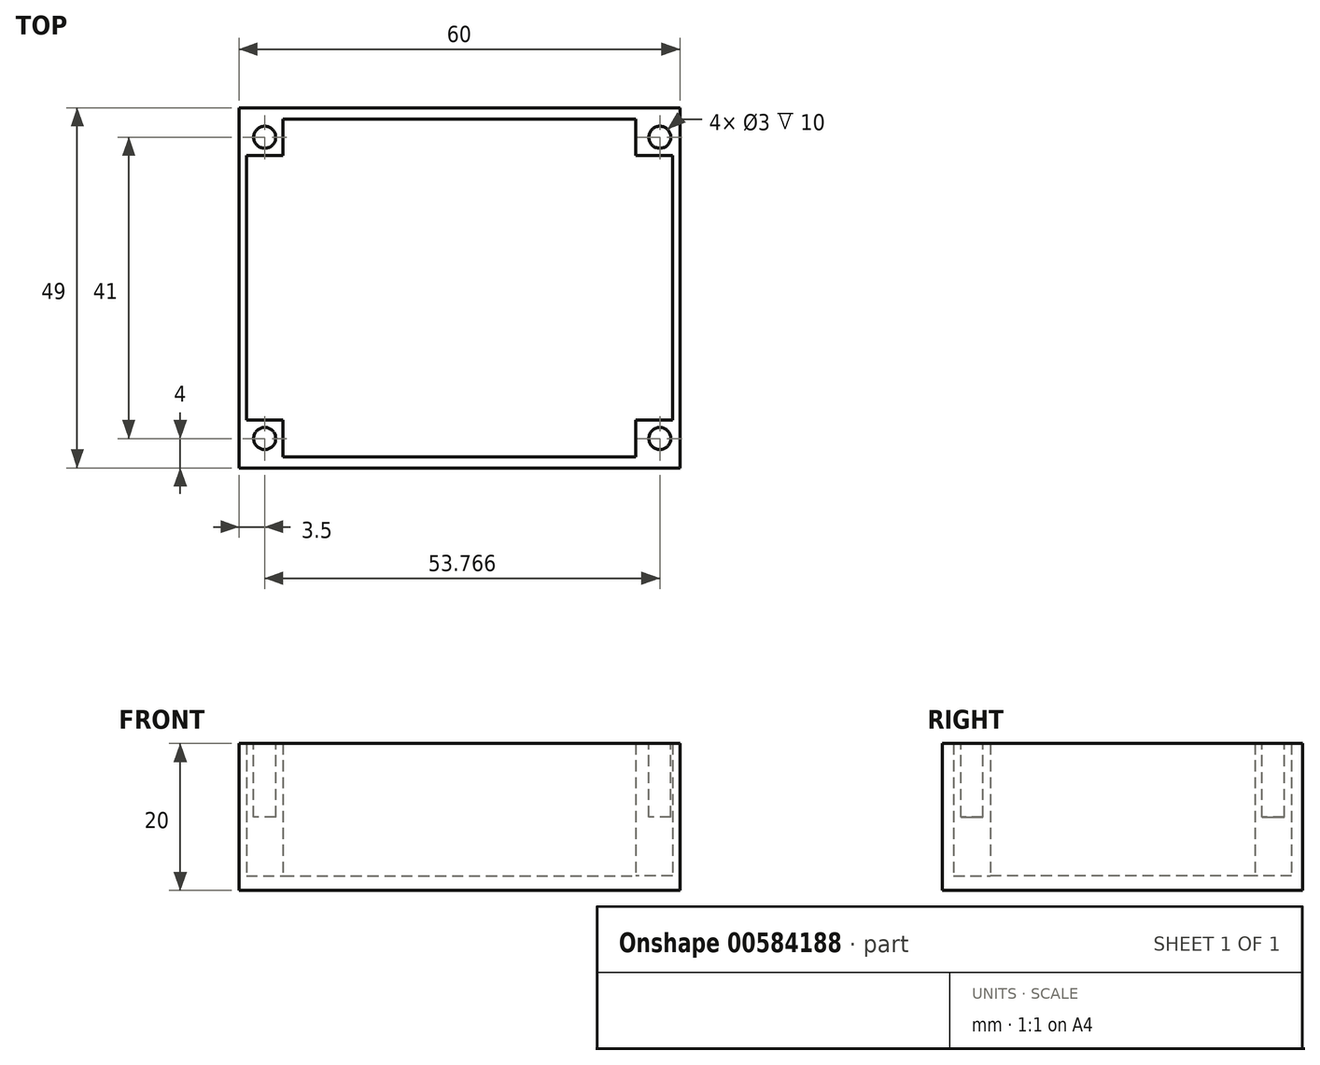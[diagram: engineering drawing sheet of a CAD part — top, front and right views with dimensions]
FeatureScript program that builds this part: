
annotation { "Feature Type Name" : "Feature", "Feature Type Description" : "" }
export const myFeature = defineFeature(function(context is Context, id is Id, definition is map)
    precondition{}
    {
        {
            var Q0;
            Q0=qCreatedBy(makeId("Top.planeOp"),FACE);
            var sketch = newSketch(context, id + "F0", { "sketchPlane" : qUnion([Q0])});
            skLineSegment(sketch, "E0.bottom", {"start": v(-30, 24.5) * mm, "end": v(30, 24.5) * mm});
            skLineSegment(sketch, "E0.top", {"start": v(-30, -24.5) * mm, "end": v(30, -24.5) * mm});
            skLineSegment(sketch, "E0.left", {"start": v(-30, 24.5) * mm, "end": v(-30, -24.5) * mm});
            skLineSegment(sketch, "E0.right", {"start": v(30, 24.5) * mm, "end": v(30, -24.5) * mm});
            skPoint(sketch, "E0.middle", {"position": v(0, 0) * mm});
            skSolve(sketch);
        }
        {
            var Q0;
            Q0=makeQuery(id+"F0.imprint","IMPRINT",FACE,{"disambiguationData":[TD([[makeQuery(id+"F0.imprint","IMPRINT",EDGE,{"derivedFrom":sQuery(id+"F0.wireOp",EDGE,"E0.bottom")}),-1.0]])]});
            extrude(context, id + "F1", {"entities" : qUnion([Q0]), "depth" : 20 * mm, "offsetDistance" : 25 * mm});
        }
        {
            var Q0;
            Q0=makeQuery(id+"F1.opExtrude","CAP_FACE",FACE,{"disambiguationData":[OSD([sQuery(id+"F0.wireOp",EDGE,"E0.bottom"),sQuery(id+"F0.wireOp",EDGE,"E0.top"),sQuery(id+"F0.wireOp",EDGE,"E0.left"),sQuery(id+"F0.wireOp",EDGE,"E0.right")])],"isStart":false});
            var sketch = newSketch(context, id + "F2", { "sketchPlane" : qUnion([Q0])});
            skLineSegment(sketch, "E1.bottom", {"start": v(-29, 23) * mm, "end": v(29, 23) * mm});
            skLineSegment(sketch, "E1.top", {"start": v(-29, -23) * mm, "end": v(29, -23) * mm});
            skLineSegment(sketch, "E1.left", {"start": v(-29, 23) * mm, "end": v(-29, -23) * mm});
            skLineSegment(sketch, "E1.right", {"start": v(29, 23) * mm, "end": v(29, -23) * mm});
            skPoint(sketch, "E1.middle", {"position": v(0, 0) * mm});
            skSolve(sketch);
        }
        {
            var Q0;
            Q0=makeQuery(id+"F2.imprint","IMPRINT",FACE,{"disambiguationData":[TD([[makeQuery(id+"F2.imprint","IMPRINT",EDGE,{"derivedFrom":sQuery(id+"F2.wireOp",EDGE,"E1.bottom")}),-1.0]])]});
            extrude(context, id + "F3", {"entities" : qUnion([Q0]), "operationType" : NewBodyOperationType.REMOVE, "oppositeDirection" : true, "depth" : 18 * mm, "offsetDistance" : 25 * mm});
        }
        {
            var Q0;
            Q0=makeQuery(id+"F3.boolean.opBoolean","COPY",FACE,{"derivedFrom":makeQuery(id+"F3.opExtrude","CAP_FACE",FACE,{"disambiguationData":[OSD([sQuery(id+"F2.wireOp",EDGE,"E1.bottom"),sQuery(id+"F2.wireOp",EDGE,"E1.top"),sQuery(id+"F2.wireOp",EDGE,"E1.left"),sQuery(id+"F2.wireOp",EDGE,"E1.right")])],"isStart":false})});
            var sketch = newSketch(context, id + "F4", { "sketchPlane" : qUnion([Q0])});
            skLineSegment(sketch, "E2.bottom", {"start": v(29, 23) * mm, "end": v(24, 23) * mm});
            skLineSegment(sketch, "E2.top", {"start": v(29, 18) * mm, "end": v(24, 18) * mm});
            skLineSegment(sketch, "E2.left", {"start": v(29, 23) * mm, "end": v(29, 18) * mm});
            skLineSegment(sketch, "E2.right", {"start": v(24, 23) * mm, "end": v(24, 18) * mm});
            skLineSegment(sketch, "E3.bottom", {"start": v(29, -23) * mm, "end": v(24, -23) * mm});
            skLineSegment(sketch, "E3.top", {"start": v(29, -18) * mm, "end": v(24, -18) * mm});
            skLineSegment(sketch, "E3.left", {"start": v(29, -23) * mm, "end": v(29, -18) * mm});
            skLineSegment(sketch, "E3.right", {"start": v(24, -23) * mm, "end": v(24, -18) * mm});
            skLineSegment(sketch, "E4.bottom", {"start": v(-29, -23) * mm, "end": v(-24, -23) * mm});
            skLineSegment(sketch, "E4.top", {"start": v(-29, -18) * mm, "end": v(-24, -18) * mm});
            skLineSegment(sketch, "E4.left", {"start": v(-29, -23) * mm, "end": v(-29, -18) * mm});
            skLineSegment(sketch, "E4.right", {"start": v(-24, -23) * mm, "end": v(-24, -18) * mm});
            skLineSegment(sketch, "E5.bottom", {"start": v(-29, 23) * mm, "end": v(-24, 23) * mm});
            skLineSegment(sketch, "E5.top", {"start": v(-29, 18) * mm, "end": v(-24, 18) * mm});
            skLineSegment(sketch, "E5.left", {"start": v(-29, 23) * mm, "end": v(-29, 18) * mm});
            skLineSegment(sketch, "E5.right", {"start": v(-24, 23) * mm, "end": v(-24, 18) * mm});
            skSolve(sketch);
        }
        {
            var Q0;
            Q0=makeQuery(id+"F4.imprint","IMPRINT",FACE,{"disambiguationData":[TD([[makeQuery(id+"F4.imprint","IMPRINT",EDGE,{"derivedFrom":sQuery(id+"F4.wireOp",EDGE,"E4.bottom")}),1.0]])]});
            var Q1;
            Q1=makeQuery(id+"F4.imprint","IMPRINT",FACE,{"disambiguationData":[TD([[makeQuery(id+"F4.imprint","IMPRINT",EDGE,{"derivedFrom":sQuery(id+"F4.wireOp",EDGE,"E3.bottom")}),1.0]])]});
            var Q2;
            Q2=makeQuery(id+"F4.imprint","IMPRINT",FACE,{"disambiguationData":[TD([[makeQuery(id+"F4.imprint","IMPRINT",EDGE,{"derivedFrom":sQuery(id+"F4.wireOp",EDGE,"E5.bottom")}),-1.0]])]});
            var Q3;
            Q3=makeQuery(id+"F4.imprint","IMPRINT",FACE,{"disambiguationData":[TD([[makeQuery(id+"F4.imprint","IMPRINT",EDGE,{"derivedFrom":sQuery(id+"F4.wireOp",EDGE,"E2.bottom")}),-1.0]])]});
            extrude(context, id + "F5", {"entities" : qUnion([Q0, Q1, Q2, Q3]), "operationType" : NewBodyOperationType.ADD, "depth" : 18 * mm, "offsetDistance" : 25 * mm});
        }
        {
            var Q0;
            Q0=makeQuery(id+"F5.boolean.opBoolean","MERGE",FACE,{"derivedFrom":[makeQuery(id+"F1.opExtrude","CAP_FACE",FACE,{"disambiguationData":[OSD([sQuery(id+"F0.wireOp",EDGE,"E0.bottom"),sQuery(id+"F0.wireOp",EDGE,"E0.top"),sQuery(id+"F0.wireOp",EDGE,"E0.left"),sQuery(id+"F0.wireOp",EDGE,"E0.right")])],"isStart":false}),makeQuery(id+"F5.opExtrude","CAP_FACE",FACE,{"disambiguationData":[OSD([sQuery(id+"F4.wireOp",EDGE,"E2.bottom"),sQuery(id+"F4.wireOp",EDGE,"E2.top"),sQuery(id+"F4.wireOp",EDGE,"E2.left"),sQuery(id+"F4.wireOp",EDGE,"E2.right")])],"isStart":false}),makeQuery(id+"F5.opExtrude","CAP_FACE",FACE,{"disambiguationData":[OSD([sQuery(id+"F4.wireOp",EDGE,"E3.bottom"),sQuery(id+"F4.wireOp",EDGE,"E3.top"),sQuery(id+"F4.wireOp",EDGE,"E3.left"),sQuery(id+"F4.wireOp",EDGE,"E3.right")])],"isStart":false}),makeQuery(id+"F5.opExtrude","CAP_FACE",FACE,{"disambiguationData":[OSD([sQuery(id+"F4.wireOp",EDGE,"E4.bottom"),sQuery(id+"F4.wireOp",EDGE,"E4.top"),sQuery(id+"F4.wireOp",EDGE,"E4.left"),sQuery(id+"F4.wireOp",EDGE,"E4.right")])],"isStart":false}),makeQuery(id+"F5.opExtrude","CAP_FACE",FACE,{"disambiguationData":[OSD([sQuery(id+"F4.wireOp",EDGE,"E5.bottom"),sQuery(id+"F4.wireOp",EDGE,"E5.top"),sQuery(id+"F4.wireOp",EDGE,"E5.left"),sQuery(id+"F4.wireOp",EDGE,"E5.right")])],"isStart":false})]});
            var sketch = newSketch(context, id + "F6", { "sketchPlane" : qUnion([Q0])});
            skCircle(sketch, "E6", {"center": v(-26.5, -20.5) * mm, "radius": 1.5 * mm});
            skPoint(sketch, "E6.centerSnap0", {"position": v(-24, -20.5) * mm});
            skPoint(sketch, "E6.centerSnap1", {"position": v(-26.5, -18) * mm});
            skCircle(sketch, "E7", {"center": v(-26.5, 20.5) * mm, "radius": 1.5 * mm});
            skPoint(sketch, "E7.centerSnap0", {"position": v(-24, 20.5) * mm});
            skPoint(sketch, "E7.centerSnap1", {"position": v(-26.5, 18) * mm});
            skCircle(sketch, "E8", {"center": v(27.27, 20.5) * mm, "radius": 1.5 * mm});
            skCircle(sketch, "E9", {"center": v(27.27, -20.5) * mm, "radius": 1.5 * mm});
            skPoint(sketch, "E9.centerSnap0", {"position": v(24, -20.5) * mm});
            skSolve(sketch);
        }
        {
            var Q0;
            Q0=makeQuery(id+"F6.imprint","IMPRINT",FACE,{"disambiguationData":[TD([[makeQuery(id+"F6.imprint","IMPRINT",EDGE,{"derivedFrom":sQuery(id+"F6.wireOp",EDGE,"E6")}),1.0]])]});
            var Q1;
            Q1=makeQuery(id+"F6.imprint","IMPRINT",FACE,{"disambiguationData":[TD([[makeQuery(id+"F6.imprint","IMPRINT",EDGE,{"derivedFrom":sQuery(id+"F6.wireOp",EDGE,"E7")}),1.0]])]});
            var Q2;
            Q2=makeQuery(id+"F6.imprint","IMPRINT",FACE,{"disambiguationData":[TD([[makeQuery(id+"F6.imprint","IMPRINT",EDGE,{"derivedFrom":sQuery(id+"F6.wireOp",EDGE,"E8")}),1.0]])]});
            var Q3;
            Q3=makeQuery(id+"F6.imprint","IMPRINT",FACE,{"disambiguationData":[TD([[makeQuery(id+"F6.imprint","IMPRINT",EDGE,{"derivedFrom":sQuery(id+"F6.wireOp",EDGE,"E9")}),1.0]])]});
            extrude(context, id + "F7", {"entities" : qUnion([Q0, Q1, Q2, Q3]), "operationType" : NewBodyOperationType.REMOVE, "oppositeDirection" : true, "depth" : 10 * mm, "offsetDistance" : 25 * mm});
        }
    });
